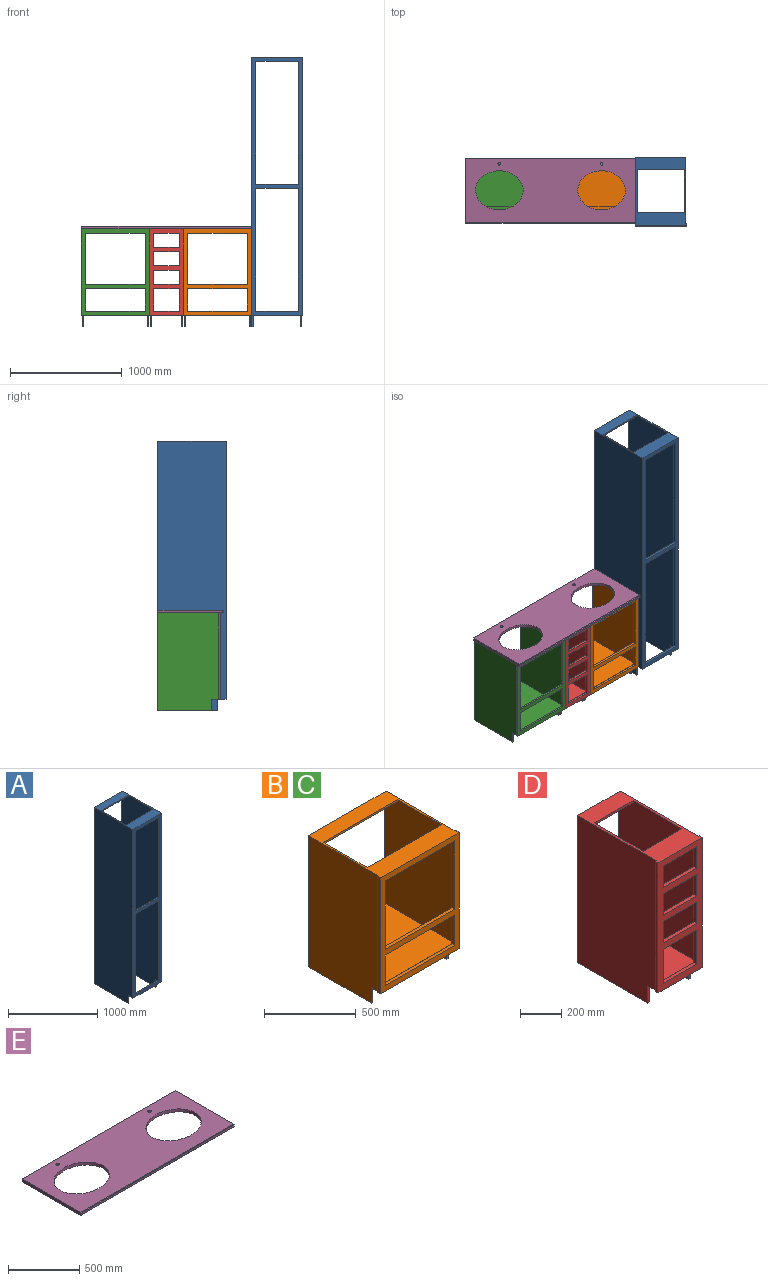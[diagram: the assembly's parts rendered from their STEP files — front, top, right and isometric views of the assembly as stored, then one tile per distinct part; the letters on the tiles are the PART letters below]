
ASSEMBLY  parts=5 mates=6
PART A: 27 faces, bbox 457.2x609.6x2413 mm
  f0: plane 1098.55x19.05mm, normal (1,0,0), area 20927.4mm2, adj f5,f9,f14,f25
  f1: plane 1098.55x19.05mm, normal (-1,0,0), area 20927.4mm2, adj f5,f9,f14,f25
  f2: plane 2413x590.55mm, normal (-1,0,0), area 1416610.1mm2, adj f5,f10,f12,f16,f18,f19,f20,f21
  f3: plane 2413x609.6mm, normal (-1,0,0), area 1463222.9mm2, adj f10,f12,f14,f15,f16,f23
  f4: plane 2413x590.55mm, normal (1,0,0), area 1416610.1mm2, adj f5,f10,f12,f15,f16,f19,f20,f21
  f5: plane 2298.7x425.45mm, normal (0,1,0), area 140886.8mm2, adj f0,f1,f2,f4,f7,f8,f9,f10
  f6: plane 2311.4x6.35mm, normal (0,1,0), area 14677.4mm2, adj f10,f11,f12,f17
  f7: plane 381x19.05mm, normal (0,0,1), area 7258.1mm2, adj f5,f8,f13,f14
  f8: plane 1098.55x19.05mm, normal (1,0,0), area 20927.4mm2, adj f5,f7,f14,f26
  f9: plane 381x19.05mm, normal (0,0,-1), area 7258.1mm2, adj f0,f1,f5,f14
  f10: plane 457.2x76.2mm, normal (0,0,-1), area 10161.3mm2, adj f2,f3,f4,f5,f6,f11,f14,f17
  f11: plane 2311.4x19.05mm, normal (1,0,0), area 44032.2mm2, adj f6,f10,f12,f14
  f12: plane 609.6x457.2mm, normal (0,0,1), area 110161.1mm2, adj f2,f3,f4,f6,f11,f14,f16,f17
  f13: plane 1098.55x19.05mm, normal (-1,0,0), area 20927.4mm2, adj f5,f7,f14,f26
  f14: plane 2311.4x457.2mm, normal (0,-1,0), area 219677mm2, adj f0,f1,f3,f7,f8,f9,f10,f11
  f15: plane 533.4x12.7mm, normal (0,0,-1), area 6774.2mm2, adj f3,f4,f16,f23
  f16: plane 2413x450.85mm, normal (0,1,0), area 66693.4mm2, adj f2,f3,f4,f12,f15,f17,f18,f21
  f17: plane 2413x590.55mm, normal (1,0,0), area 1419190.7mm2, adj f6,f10,f12,f16,f18,f24
  f18: plane 533.4x12.7mm, normal (0,0,-1), area 6774.2mm2, adj f2,f16,f17,f24
  f19: plane 425.45x12.7mm, normal (0,1,0), area 5403.2mm2, adj f2,f4,f12,f20
  f20: plane 425.45x101.6mm, normal (0,0,-1), area 43225.7mm2, adj f2,f4,f5,f19
  f21: plane 425.45x101.6mm, normal (0,0,-1), area 43225.7mm2, adj f2,f4,f16,f22
  f22: plane 425.45x12.7mm, normal (0,-1,0), area 5403.2mm2, adj f2,f4,f12,f21
  f23: plane 101.6x12.7mm, normal (0,-1,0), area 1290.3mm2, adj f3,f4,f10,f15
  f24: plane 101.6x12.7mm, normal (0,-1,0), area 1290.3mm2, adj f2,f10,f17,f18
  f25: plane 381x19.05mm, normal (0,0,1), area 7258.1mm2, adj f0,f1,f5,f14
  f26: plane 381x19.05mm, normal (0,0,-1), area 7258.1mm2, adj f5,f8,f13,f14
PART B: 34 faces, bbox 609.6x558.8x876.3 mm
  f0: plane 457.2x19.05mm, normal (1,0,0), area 8709.7mm2, adj f6,f12,f18,f32
  f1: plane 457.2x19.05mm, normal (-1,0,0), area 8709.7mm2, adj f6,f12,f18,f32
  f2: plane 876.3x539.75mm, normal (-1,0,0), area 467176.5mm2, adj f9,f13,f15,f19,f25,f31
  f3: plane 539.75x123.83mm, normal (1,0,0), area 61028.1mm2, adj f7,f13,f19,f20,f25,f31
  f4: plane 539.75x123.83mm, normal (-1,0,0), area 61028.1mm2, adj f7,f13,f20,f21,f25,f30
  f5: plane 739.78x539.75mm, normal (-1,0,0), area 396712.9mm2, adj f6,f15,f23,f25,f26,f27,f28,f29
  f6: plane 727.08x571.5mm, normal (0,1,0), area 63266mm2, adj f0,f1,f5,f10,f11,f12,f17,f23
  f7: plane 571.5x22.23mm, normal (0,1,0), area 12701.6mm2, adj f3,f4,f13,f20
  f8: plane 774.7x6.35mm, normal (0,1,0), area 4919.3mm2, adj f13,f14,f15,f22
  f9: plane 774.7x6.35mm, normal (0,1,0), area 4919.3mm2, adj f2,f13,f15,f16
  f10: plane 533.4x19.05mm, normal (0,0,1), area 10161.3mm2, adj f6,f11,f17,f18
  f11: plane 203.2x19.05mm, normal (1,0,0), area 3871mm2, adj f6,f10,f18,f33
  f12: plane 533.4x19.05mm, normal (0,0,-1), area 10161.3mm2, adj f0,f1,f6,f18
  f13: plane 609.6x76.2mm, normal (0,0,-1), area 13064.5mm2, adj f2,f3,f4,f7,f8,f9,f14,f16
  f14: plane 774.7x19.05mm, normal (1,0,0), area 14758mm2, adj f8,f13,f15,f18
  f15: plane 609.6x558.8mm, normal (0,0,1), area 141451.3mm2, adj f2,f5,f8,f9,f14,f16,f18,f22
  f16: plane 774.7x19.05mm, normal (-1,0,0), area 14758mm2, adj f9,f13,f15,f18
  f17: plane 203.2x19.05mm, normal (-1,0,0), area 3871mm2, adj f6,f10,f18,f33
  f18: plane 774.7x609.6mm, normal (0,-1,0), area 119999.8mm2, adj f0,f1,f10,f11,f12,f13,f14,f15
  f19: plane 482.6x12.7mm, normal (0,0,-1), area 6129mm2, adj f2,f3,f25,f31
  f20: plane 571.5x539.75mm, normal (0,0,-1), area 308467.1mm2, adj f3,f4,f7,f25
  f21: plane 482.6x12.7mm, normal (0,0,-1), area 6129mm2, adj f4,f22,f25,f30
  f22: plane 876.3x539.75mm, normal (1,0,0), area 467176.5mm2, adj f8,f13,f15,f21,f25,f30
  f23: plane 571.5x539.75mm, normal (0,0,1), area 308467.1mm2, adj f5,f6,f24,f25
  f24: plane 739.78x539.75mm, normal (1,0,0), area 396712.9mm2, adj f6,f15,f23,f25,f26,f27,f28,f29
  f25: plane 876.3x596.9mm, normal (0,1,0), area 36774.1mm2, adj f2,f3,f4,f5,f15,f19,f20,f21
  f26: plane 571.5x12.7mm, normal (0,1,0), area 7258mm2, adj f5,f15,f24,f27
  f27: plane 571.5x101.6mm, normal (0,0,-1), area 58064.4mm2, adj f5,f6,f24,f26
  f28: plane 571.5x101.6mm, normal (0,0,-1), area 58064.4mm2, adj f5,f24,f25,f29
  f29: plane 571.5x12.7mm, normal (0,-1,0), area 7258mm2, adj f5,f15,f24,f28
  f30: plane 101.6x12.7mm, normal (0,-1,0), area 1290.3mm2, adj f4,f13,f21,f22
  f31: plane 101.6x12.7mm, normal (0,-1,0), area 1290.3mm2, adj f2,f3,f13,f19
  f32: plane 533.4x19.05mm, normal (0,0,1), area 10161.3mm2, adj f0,f1,f6,f18
  f33: plane 533.4x19.05mm, normal (0,0,-1), area 10161.3mm2, adj f6,f11,f17,f18
PART C: same geometry as B
PART D: 42 faces, bbox 304.8x558.8x876.3 mm
  f0: plane 127x19.05mm, normal (1,0,0), area 2419.3mm2, adj f10,f22,f39,f40
  f1: plane 127x19.05mm, normal (-1,0,0), area 2419.3mm2, adj f10,f22,f39,f40
  f2: plane 127x19.05mm, normal (1,0,0), area 2419.3mm2, adj f10,f22,f37,f38
  f3: plane 127x19.05mm, normal (-1,0,0), area 2419.3mm2, adj f10,f22,f37,f38
  f4: plane 127x19.05mm, normal (1,0,0), area 2419.3mm2, adj f10,f16,f22,f36
  f5: plane 127x19.05mm, normal (-1,0,0), area 2419.3mm2, adj f10,f16,f22,f36
  f6: plane 876.3x539.75mm, normal (-1,0,0), area 467176.5mm2, adj f13,f17,f19,f23,f29,f35
  f7: plane 539.75x123.83mm, normal (1,0,0), area 61028.1mm2, adj f11,f17,f23,f24,f29,f35
  f8: plane 539.75x123.83mm, normal (-1,0,0), area 61028.1mm2, adj f11,f17,f24,f25,f29,f34
  f9: plane 739.78x539.75mm, normal (-1,0,0), area 396712.9mm2, adj f10,f19,f27,f29,f30,f31,f32,f33
  f10: plane 727.08x266.7mm, normal (0,1,0), area 60362.8mm2, adj f0,f1,f2,f3,f4,f5,f9,f14
  f11: plane 266.7x22.23mm, normal (0,1,0), area 5927.4mm2, adj f7,f8,f17,f24
  f12: plane 774.7x6.35mm, normal (0,1,0), area 4919.3mm2, adj f17,f18,f19,f26
  f13: plane 774.7x6.35mm, normal (0,1,0), area 4919.3mm2, adj f6,f17,f19,f20
  f14: plane 228.6x19.05mm, normal (0,0,1), area 4354.8mm2, adj f10,f15,f21,f22
  f15: plane 203.2x19.05mm, normal (1,0,0), area 3871mm2, adj f10,f14,f22,f41
  f16: plane 228.6x19.05mm, normal (0,0,-1), area 4354.8mm2, adj f4,f5,f10,f22
  f17: plane 304.8x76.2mm, normal (0,0,-1), area 7258.1mm2, adj f6,f7,f8,f11,f12,f13,f18,f20
  f18: plane 774.7x19.05mm, normal (1,0,0), area 14758mm2, adj f12,f17,f19,f22
  f19: plane 558.8x304.8mm, normal (0,0,1), area 73709.5mm2, adj f6,f9,f12,f13,f18,f20,f22,f26
  f20: plane 774.7x19.05mm, normal (-1,0,0), area 14758mm2, adj f13,f17,f19,f22
  f21: plane 203.2x19.05mm, normal (-1,0,0), area 3871mm2, adj f10,f14,f22,f41
  f22: plane 774.7x304.8mm, normal (0,-1,0), area 102580.4mm2, adj f0,f1,f2,f3,f4,f5,f14,f15
  f23: plane 482.6x12.7mm, normal (0,0,-1), area 6129mm2, adj f6,f7,f29,f35
  f24: plane 539.75x266.7mm, normal (0,0,-1), area 143951.3mm2, adj f7,f8,f11,f29
  f25: plane 482.6x12.7mm, normal (0,0,-1), area 6129mm2, adj f8,f26,f29,f34
  f26: plane 876.3x539.75mm, normal (1,0,0), area 467176.5mm2, adj f12,f17,f19,f25,f29,f34
  f27: plane 539.75x266.7mm, normal (0,0,1), area 143951.3mm2, adj f9,f10,f28,f29
  f28: plane 739.78x539.75mm, normal (1,0,0), area 396712.9mm2, adj f10,f19,f27,f29,f30,f31,f32,f33
  f29: plane 876.3x292.1mm, normal (0,1,0), area 29032.2mm2, adj f6,f7,f8,f9,f19,f23,f24,f25
  f30: plane 266.7x12.7mm, normal (0,1,0), area 3387.1mm2, adj f9,f19,f28,f31
  f31: plane 266.7x101.6mm, normal (0,0,-1), area 27096.7mm2, adj f9,f10,f28,f30
  f32: plane 266.7x101.6mm, normal (0,0,-1), area 27096.7mm2, adj f9,f28,f29,f33
  f33: plane 266.7x12.7mm, normal (0,-1,0), area 3387.1mm2, adj f9,f19,f28,f32
  f34: plane 101.6x12.7mm, normal (0,-1,0), area 1290.3mm2, adj f8,f17,f25,f26
  f35: plane 101.6x12.7mm, normal (0,-1,0), area 1290.3mm2, adj f6,f7,f17,f23
  f36: plane 228.6x19.05mm, normal (0,0,1), area 4354.8mm2, adj f4,f5,f10,f22
  f37: plane 228.6x19.05mm, normal (0,0,-1), area 4354.8mm2, adj f2,f3,f10,f22
  f38: plane 228.6x19.05mm, normal (0,0,1), area 4354.8mm2, adj f2,f3,f10,f22
  f39: plane 228.6x19.05mm, normal (0,0,-1), area 4354.8mm2, adj f0,f1,f10,f22
  f40: plane 228.6x19.05mm, normal (0,0,1), area 4354.8mm2, adj f0,f1,f10,f22
  f41: plane 228.6x19.05mm, normal (0,0,-1), area 4354.8mm2, adj f10,f15,f21,f22
PART E: 13 faces, bbox 1524x584.2x25.4 mm
  f0: plane 584.2x25.4mm, normal (1,0,0), area 14828.9mm2, adj f1,f3,f4,f5,f6,f7
  f1: plane 1524x25.4mm, normal (0,1,0), area 38709.6mm2, adj f0,f2,f4,f5
  f2: plane 579.44x25.4mm, normal (-1,0,0), area 14717.7mm2, adj f1,f4,f5,f8
  f3: plane 1519.24x15.88mm, normal (0,-1,0), area 24117.9mm2, adj f0,f6,f7,f8
  f4: plane 1524x579.44mm, normal (0,0,1), area 648647.2mm2, adj f0,f1,f2,f6,f9,f10,f11,f12
  f5: plane 1524x579.44mm, normal (0,0,-1), area 648647.2mm2, adj f0,f1,f2,f7,f9,f10,f11,f12
  f6: cylinder r=4.76mm len=1524mm, axis (-1,0,0), area 11388mm2, adj f0,f3,f4,f8
  f7: cylinder r=4.76mm len=1524mm, axis (1,0,0), area 11388mm2, adj f0,f3,f5,f8
  f8: cylinder r=4.76mm len=25.4mm, axis (0,0,1), area 164.1mm2, adj f2,f3,f6,f7
  f9: cylinder r=12.7mm len=25.4mm, axis (0,0,1), area 2026.8mm2, adj f4,f5
  f10: extruded ~425.45x349.25mm, area 30984mm2, adj f4,f5
  f11: extruded ~425.45x349.25mm, area 30984mm2, adj f4,f5
  f12: cylinder r=12.7mm len=25.4mm, axis (0,0,1), area 2026.8mm2, adj f4,f5
PLACE A t=(1371.6,-50.8,0)mm
PLACE B t=(914.4,0,0)mm
PLACE C at identity fixed
PLACE D t=(304.8,0,0)mm
PLACE E t=(914.4,539.75,876.3)mm
MATE planar B.f21 <-> A.f15  axis (0,0,-1) through (901.7,298.45,0)mm
MATE planar B.f14 <-> A.f3  axis (1,0,0) through (914.4,-9.53,488.95)mm
MATE fastened E.f1 <-> B.f25  axis (0,1,0) through (914.4,539.75,876.3)mm
MATE fastened D.f17 <-> B.f13  axis (0,0,-1) through (304.8,-19.05,101.6)mm
MATE fastened C.f13 <-> D.f17  axis (0,0,-1) through (0,-19.05,101.6)mm
MATE planar A.f16 <-> B.f25  axis (0,1,0) through (914.4,539.75,0)mm
